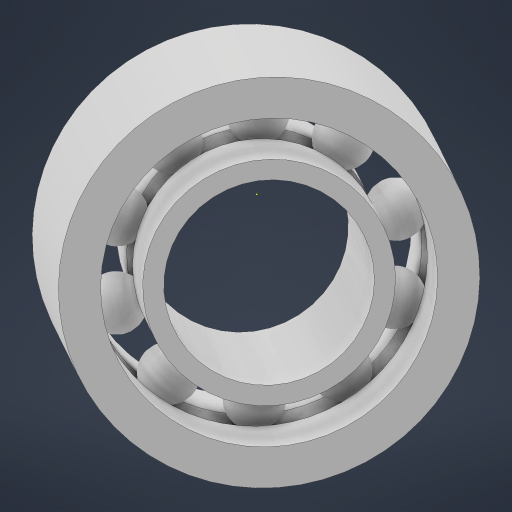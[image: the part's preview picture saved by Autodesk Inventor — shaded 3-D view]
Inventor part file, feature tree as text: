
AUTODESK INVENTOR PART (.ipt)
format: ipt  version: 2023 (Build 270158000, 158)  size: 380,416 bytes
history: native  units: mm
features: sketch x6, revolve x2, pattern_circular x1, sweep x1, hole x1
ambient origin geometry x8: Origin, YZ Plane, XZ Plane, XY Plane, X Axis, Y Axis, Z Axis, Center Point
bodies: Solid1 (feature_tree)
feature tree (11):
  revolve  "Revolution1"  [1 undecoded]
  revolve  "Revolution2"  [1 undecoded]
  sketch  "Sketch4"  dims[d8=90.0deg]
  pattern_circular  "Circular Pattern1"  Count=10 Angle=360.0deg
  sketch  "Sketch5"  dims[d9=3.0mm]
  sweep  "Sweep1"
  hole  "Hole1"  [1 undecoded]
  sketch  "Sketch2"  dims[d4=10.0mm d5=6.0mm]
  sketch  "Sketch3"  dims[d6=3.0mm d7=4.0mm]
  sketch  "Sketch7"  dims[d10=360.0deg d11=100.0mm d12=360.0deg]
  sketch  "Sketch8"  dims[d14=10.0mm d15=2.0mm d16=12.0mm d17=0.0mm d18=0.0mm d19=10.0mm d20=6.0mm d21=4.0mm d22=2.0mm d23=90.0deg d24=8.0mm d25=20.594885mm]
note: 3 required parameter values undecoded (feature->parameter linkage not recoverable at this tier; creation-order binding heuristic only, values carry confidence <= 0.55)